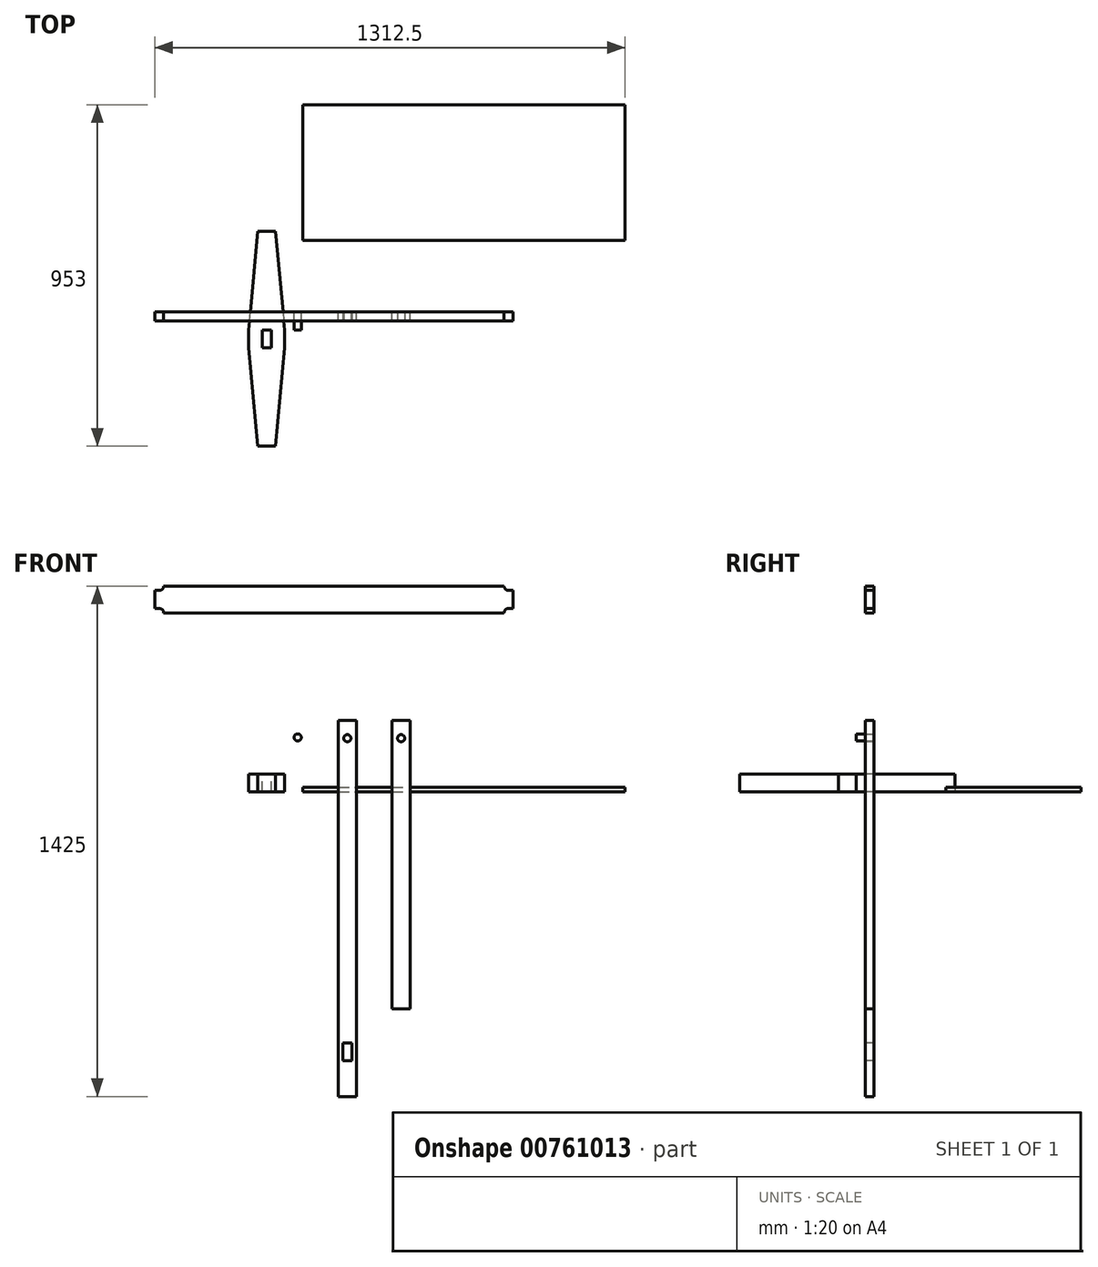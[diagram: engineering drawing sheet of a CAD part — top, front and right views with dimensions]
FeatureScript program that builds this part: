
annotation { "Feature Type Name" : "Feature", "Feature Type Description" : "" }
export const myFeature = defineFeature(function(context is Context, id is Id, definition is map)
    precondition{}
    {
        {
            var Q0;
            Q0=qCreatedBy(makeId("Top.planeOp"),FACE);
            var sketch = newSketch(context, id + "F0", { "sketchPlane" : qUnion([Q0])});
            skLineSegment(sketch, "E0", {"start": v(-125, 225) * mm, "end": v(-75, 225) * mm});
            skLineSegment(sketch, "E1", {"start": v(-75, 225) * mm, "end": v(-50, -50) * mm});
            skLineSegment(sketch, "E2", {"start": v(-50, -50) * mm, "end": v(-50, -100) * mm});
            skLineSegment(sketch, "E3", {"start": v(-50, -100) * mm, "end": v(-75, -375) * mm});
            skLineSegment(sketch, "E4", {"start": v(-75, -375) * mm, "end": v(-125, -375) * mm});
            skLineSegment(sketch, "E5", {"start": v(-125, -375) * mm, "end": v(-150, -100) * mm});
            skLineSegment(sketch, "E6", {"start": v(-150, -100) * mm, "end": v(-150, -50) * mm});
            skLineSegment(sketch, "E7", {"start": v(-150, -50) * mm, "end": v(-125, 225) * mm});
            skSolve(sketch);
        }
        {
            var Q0;
            Q0=makeQuery(id+"F0.imprint","IMPRINT",FACE,{"disambiguationData":[TD([[makeQuery(id+"F0.imprint","IMPRINT",EDGE,{"derivedFrom":sQuery(id+"F0.wireOp",EDGE,"E0")}),-1.0]])]});
            extrude(context, id + "F1", {"entities" : qUnion([Q0]), "depth" : 50 * mm, "offsetDistance" : 25 * mm});
        }
        {
            var Q0;
            Q0=makeQuery(id+"F1.opExtrude","CAP_FACE",FACE,{"disambiguationData":[OSD([sQuery(id+"F0.wireOp",EDGE,"E0"),sQuery(id+"F0.wireOp",EDGE,"E1"),sQuery(id+"F0.wireOp",EDGE,"E2"),sQuery(id+"F0.wireOp",EDGE,"E3"),sQuery(id+"F0.wireOp",EDGE,"E4"),sQuery(id+"F0.wireOp",EDGE,"E5"),sQuery(id+"F0.wireOp",EDGE,"E6"),sQuery(id+"F0.wireOp",EDGE,"E7")])],"isStart":false});
            var sketch = newSketch(context, id + "F2", { "sketchPlane" : qUnion([Q0])});
            skLineSegment(sketch, "E8", {"start": v(-150, -50) * mm, "end": v(-50, -100) * mm, "construction": true});
            skLineSegment(sketch, "E9", {"start": v(-50, -50) * mm, "end": v(-150, -100) * mm, "construction": true});
            skLineSegment(sketch, "E10.bottom", {"start": v(-87.5, -50) * mm, "end": v(-112.5, -50) * mm});
            skLineSegment(sketch, "E10.top", {"start": v(-87.5, -100) * mm, "end": v(-112.5, -100) * mm});
            skLineSegment(sketch, "E10.left", {"start": v(-87.5, -50) * mm, "end": v(-87.5, -100) * mm});
            skLineSegment(sketch, "E10.right", {"start": v(-112.5, -50) * mm, "end": v(-112.5, -100) * mm});
            skPoint(sketch, "E10.middle", {"position": v(-100, -75) * mm});
            skSolve(sketch);
        }
        {
            var Q0;
            Q0=makeQuery(id+"F2.imprint","IMPRINT",FACE,{"disambiguationData":[TD([[makeQuery(id+"F2.imprint","IMPRINT",EDGE,{"derivedFrom":sQuery(id+"F2.wireOp",EDGE,"E10.bottom")}),1.0]])]});
            extrude(context, id + "F3", {"entities" : qUnion([Q0]), "operationType" : NewBodyOperationType.REMOVE, "endBound" : BoundingType.UP_TO_NEXT, "oppositeDirection" : true, "depth" : 25 * mm, "offsetDistance" : 25 * mm});
        }
        {
            var Q0;
            Q0=qCreatedBy(makeId("Front.planeOp"),FACE);
            var sketch = newSketch(context, id + "F4", { "sketchPlane" : qUnion([Q0])});
            skLineSegment(sketch, "E11.bottom", {"start": v(100, 200) * mm, "end": v(150, 200) * mm});
            skLineSegment(sketch, "E11.top", {"start": v(100, -850) * mm, "end": v(150, -850) * mm});
            skLineSegment(sketch, "E11.left", {"start": v(100, 200) * mm, "end": v(100, -850) * mm});
            skLineSegment(sketch, "E11.right", {"start": v(150, 200) * mm, "end": v(150, -850) * mm});
            skSolve(sketch);
        }
        {
            var Q0;
            Q0=makeQuery(id+"F4.imprint","IMPRINT",FACE,{"disambiguationData":[TD([[makeQuery(id+"F4.imprint","IMPRINT",EDGE,{"derivedFrom":sQuery(id+"F4.wireOp",EDGE,"E11.bottom")}),-1.0]])]});
            extrude(context, id + "F5", {"entities" : qUnion([Q0]), "depth" : 25 * mm, "offsetDistance" : 25 * mm});
        }
        {
            var Q0;
            Q0=makeQuery(id+"F5.opExtrude","CAP_FACE",FACE,{"disambiguationData":[OSD([sQuery(id+"F4.wireOp",EDGE,"E11.bottom"),sQuery(id+"F4.wireOp",EDGE,"E11.top"),sQuery(id+"F4.wireOp",EDGE,"E11.left"),sQuery(id+"F4.wireOp",EDGE,"E11.right")])],"isStart":false});
            var sketch = newSketch(context, id + "F6", { "sketchPlane" : qUnion([Q0])});
            skLineSegment(sketch, "E12.bottom", {"start": v(112.5, -700) * mm, "end": v(137.5, -700) * mm});
            skLineSegment(sketch, "E12.top", {"start": v(112.5, -750) * mm, "end": v(137.5, -750) * mm});
            skLineSegment(sketch, "E12.left", {"start": v(112.5, -700) * mm, "end": v(112.5, -750) * mm});
            skLineSegment(sketch, "E12.right", {"start": v(137.5, -700) * mm, "end": v(137.5, -750) * mm});
            skLineSegment(sketch, "E13", {"start": v(125, 200) * mm, "end": v(125, -850) * mm, "construction": true});
            skCircle(sketch, "E14", {"center": v(125, 150) * mm, "radius": 10 * mm});
            skSolve(sketch);
        }
        {
            var Q0;
            Q0=makeQuery(id+"F6.imprint","IMPRINT",FACE,{"disambiguationData":[TD([[makeQuery(id+"F6.imprint","IMPRINT",EDGE,{"derivedFrom":sQuery(id+"F6.wireOp",EDGE,"E12.bottom")}),-1.0]])]});
            var Q1;
            Q1=makeQuery(id+"F6.imprint","IMPRINT",FACE,{"disambiguationData":[TD([[makeQuery(id+"F6.imprint","IMPRINT",EDGE,{"derivedFrom":sQuery(id+"F6.wireOp",EDGE,"E14")}),1.0]])]});
            extrude(context, id + "F7", {"entities" : qUnion([Q0, Q1]), "operationType" : NewBodyOperationType.REMOVE, "endBound" : BoundingType.UP_TO_NEXT, "oppositeDirection" : true, "depth" : 25 * mm, "offsetDistance" : 25 * mm});
        }
        {
            var Q0;
            Q0=qCreatedBy(makeId("Front.planeOp"),FACE);
            var sketch = newSketch(context, id + "F8", { "sketchPlane" : qUnion([Q0])});
            skLineSegment(sketch, "E15.bottom", {"start": v(250, 200) * mm, "end": v(300, 200) * mm});
            skLineSegment(sketch, "E15.top", {"start": v(250, -605) * mm, "end": v(300, -605) * mm});
            skLineSegment(sketch, "E15.left", {"start": v(250, 200) * mm, "end": v(250, -605) * mm});
            skLineSegment(sketch, "E15.right", {"start": v(300, 200) * mm, "end": v(300, -605) * mm});
            skSolve(sketch);
        }
        {
            var Q0;
            Q0=makeQuery(id+"F8.imprint","IMPRINT",FACE,{"disambiguationData":[TD([[makeQuery(id+"F8.imprint","IMPRINT",EDGE,{"derivedFrom":sQuery(id+"F8.wireOp",EDGE,"E15.bottom")}),-1.0]])]});
            extrude(context, id + "F9", {"entities" : qUnion([Q0]), "depth" : 25 * mm, "offsetDistance" : 25 * mm});
        }
        {
            var Q0;
            Q0=makeQuery(id+"F9.opExtrude","CAP_FACE",FACE,{"disambiguationData":[OSD([sQuery(id+"F8.wireOp",EDGE,"E15.bottom"),sQuery(id+"F8.wireOp",EDGE,"E15.top"),sQuery(id+"F8.wireOp",EDGE,"E15.left"),sQuery(id+"F8.wireOp",EDGE,"E15.right")])],"isStart":false});
            var sketch = newSketch(context, id + "F10", { "sketchPlane" : qUnion([Q0])});
            skLineSegment(sketch, "E16", {"start": v(275, -605) * mm, "end": v(275, 200) * mm, "construction": true});
            skCircle(sketch, "E17", {"center": v(275, 150) * mm, "radius": 10 * mm});
            skSolve(sketch);
        }
        {
            var Q0;
            Q0=makeQuery(id+"F10.imprint","IMPRINT",FACE,{"disambiguationData":[TD([[makeQuery(id+"F10.imprint","IMPRINT",EDGE,{"derivedFrom":sQuery(id+"F10.wireOp",EDGE,"E17")}),1.0]])]});
            extrude(context, id + "F11", {"entities" : qUnion([Q0]), "operationType" : NewBodyOperationType.REMOVE, "endBound" : BoundingType.UP_TO_NEXT, "oppositeDirection" : true, "depth" : 25 * mm, "offsetDistance" : 25 * mm});
        }
        {
            var Q0;
            Q0=qCreatedBy(makeId("Front.planeOp"),FACE);
            var sketch = newSketch(context, id + "F12", { "sketchPlane" : qUnion([Q0])});
            skLineSegment(sketch, "E18", {"start": v(-412.5, 562.5) * mm, "end": v(-412.5, 512.5) * mm});
            skLineSegment(sketch, "E19", {"start": v(-412.5, 512.5) * mm, "end": v(-400, 512.5) * mm});
            skLineSegment(sketch, "E20", {"start": v(-387.5, 500) * mm, "end": v(562.5, 500) * mm});
            skLineSegment(sketch, "E21", {"start": v(575, 512.5) * mm, "end": v(587.5, 512.5) * mm});
            skLineSegment(sketch, "E22", {"start": v(587.5, 512.5) * mm, "end": v(587.5, 562.5) * mm});
            skLineSegment(sketch, "E23", {"start": v(587.5, 562.5) * mm, "end": v(575, 562.5) * mm});
            skLineSegment(sketch, "E24", {"start": v(562.5, 575) * mm, "end": v(-387.5, 575) * mm});
            skLineSegment(sketch, "E25", {"start": v(-400, 562.5) * mm, "end": v(-412.5, 562.5) * mm});
            skArc(sketch, "E26", {"start": v(-400, 562.5) * mm, "mid": v(-391.16, 566.16) * mm, "end": v(-387.5, 575) * mm});
            skArc(sketch, "E27", {"start": v(-387.5, 500) * mm, "mid": v(-391.16, 508.84) * mm, "end": v(-400, 512.5) * mm});
            skArc(sketch, "E28", {"start": v(562.5, 575) * mm, "mid": v(566.16, 566.16) * mm, "end": v(575, 562.5) * mm});
            skArc(sketch, "E29", {"start": v(575, 512.5) * mm, "mid": v(566.16, 508.84) * mm, "end": v(562.5, 500) * mm});
            skSolve(sketch);
        }
        {
            var Q0;
            Q0=makeQuery(id+"F12.imprint","IMPRINT",FACE,{"disambiguationData":[TD([[makeQuery(id+"F12.imprint","IMPRINT",EDGE,{"derivedFrom":sQuery(id+"F12.wireOp",EDGE,"E18")}),1.0]])]});
            extrude(context, id + "F13", {"entities" : qUnion([Q0]), "depth" : 25 * mm, "offsetDistance" : 25 * mm});
        }
        {
            var Q0;
            Q0=qCreatedBy(makeId("Front.planeOp"),FACE);
            var sketch = newSketch(context, id + "F14", { "sketchPlane" : qUnion([Q0])});
            skCircle(sketch, "E30", {"center": v(-13.53, 152.28) * mm, "radius": 10 * mm});
            skSolve(sketch);
        }
        {
            var Q0;
            Q0=makeQuery(id+"F14.imprint","IMPRINT",FACE,{"disambiguationData":[TD([[makeQuery(id+"F14.imprint","IMPRINT",EDGE,{"derivedFrom":sQuery(id+"F14.wireOp",EDGE,"E30")}),1.0]])]});
            extrude(context, id + "F15", {"entities" : qUnion([Q0]), "depth" : 50 * mm, "offsetDistance" : 25 * mm});
        }
        {
            var Q0;
            Q0=qCreatedBy(makeId("Top.planeOp"),FACE);
            var sketch = newSketch(context, id + "F16", { "sketchPlane" : qUnion([Q0])});
            skLineSegment(sketch, "E31.bottom", {"start": v(0, 200) * mm, "end": v(900, 200) * mm});
            skLineSegment(sketch, "E31.top", {"start": v(0, 578) * mm, "end": v(900, 578) * mm});
            skLineSegment(sketch, "E31.left", {"start": v(0, 200) * mm, "end": v(0, 578) * mm});
            skLineSegment(sketch, "E31.right", {"start": v(900, 200) * mm, "end": v(900, 578) * mm});
            skSolve(sketch);
        }
        {
            var Q0;
            Q0=makeQuery(id+"F16.imprint","IMPRINT",FACE,{"disambiguationData":[TD([[makeQuery(id+"F16.imprint","IMPRINT",EDGE,{"derivedFrom":sQuery(id+"F16.wireOp",EDGE,"E31.bottom")}),1.0]])]});
            extrude(context, id + "F17", {"entities" : qUnion([Q0]), "depth" : 13 * mm, "offsetDistance" : 25 * mm});
        }
    });
